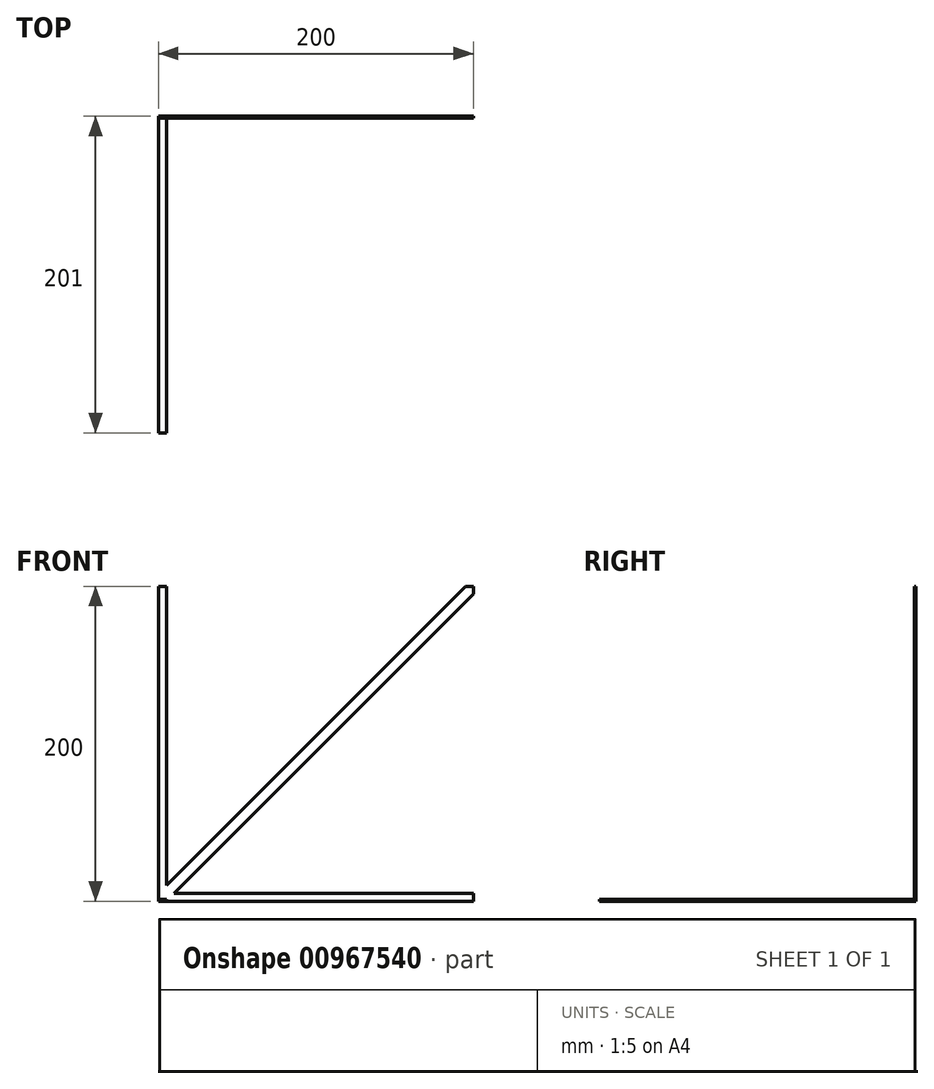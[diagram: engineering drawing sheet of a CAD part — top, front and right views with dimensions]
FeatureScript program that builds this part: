
annotation { "Feature Type Name" : "Feature", "Feature Type Description" : "" }
export const myFeature = defineFeature(function(context is Context, id is Id, definition is map)
    precondition{}
    {
        {
            var Q0;
            Q0=qCreatedBy(makeId("Front.planeOp"),FACE);
            var sketch = newSketch(context, id + "F0", { "sketchPlane" : qUnion([Q0])});
            skLineSegment(sketch, "E0.bottom", {"start": v(0, 0) * mm, "end": v(5, 0) * mm});
            skLineSegment(sketch, "E0.left", {"start": v(0, 0) * mm, "end": v(0, 5) * mm});
            skLineSegment(sketch, "E1", {"start": v(10, 5) * mm, "end": v(200, 195) * mm});
            skLineSegment(sketch, "E2", {"start": v(5, 10) * mm, "end": v(195, 200) * mm});
            skLineSegment(sketch, "E3", {"start": v(195, 200) * mm, "end": v(200, 200) * mm});
            skLineSegment(sketch, "E4", {"start": v(200, 200) * mm, "end": v(200, 195) * mm});
            skLineSegment(sketch, "E5", {"start": v(5, 0) * mm, "end": v(200, 0) * mm});
            skLineSegment(sketch, "E6", {"start": v(200, 0) * mm, "end": v(200, 5) * mm});
            skLineSegment(sketch, "E7", {"start": v(200, 5) * mm, "end": v(10, 5) * mm});
            skLineSegment(sketch, "E8", {"start": v(0, 5) * mm, "end": v(0, 200) * mm});
            skLineSegment(sketch, "E9", {"start": v(0, 200) * mm, "end": v(5, 200) * mm});
            skLineSegment(sketch, "E10", {"start": v(5, 200) * mm, "end": v(5, 10) * mm});
            skSolve(sketch);
        }
        {
            var Q0;
            Q0=makeQuery(id+"F0.imprint","IMPRINT",FACE,{"disambiguationData":[TD([[makeQuery(id+"F0.imprint","IMPRINT",EDGE,{"derivedFrom":sQuery(id+"F0.wireOp",EDGE,"E0.bottom")}),1.0]])]});
            extrude(context, id + "F1", {"entities" : qUnion([Q0]), "depth" : 1 * mm, "offsetDistance" : 25 * mm});
        }
        {
            var Q0;
            Q0=makeQuery(id+"F1.opExtrude","CAP_FACE",FACE,{"disambiguationData":[OSD([sQuery(id+"F0.wireOp",EDGE,"E0.bottom"),sQuery(id+"F0.wireOp",EDGE,"E0.left"),sQuery(id+"F0.wireOp",EDGE,"E1"),sQuery(id+"F0.wireOp",EDGE,"E2"),sQuery(id+"F0.wireOp",EDGE,"E3"),sQuery(id+"F0.wireOp",EDGE,"E4"),sQuery(id+"F0.wireOp",EDGE,"E5"),sQuery(id+"F0.wireOp",EDGE,"E6"),sQuery(id+"F0.wireOp",EDGE,"E7"),sQuery(id+"F0.wireOp",EDGE,"E8"),sQuery(id+"F0.wireOp",EDGE,"E9"),sQuery(id+"F0.wireOp",EDGE,"E10")])],"isStart":false});
            var sketch = newSketch(context, id + "F2", { "sketchPlane" : qUnion([Q0])});
            skLineSegment(sketch, "E11.bottom", {"start": v(0, 0) * mm, "end": v(5, 0) * mm});
            skLineSegment(sketch, "E11.top", {"start": v(0, 1) * mm, "end": v(5, 1) * mm});
            skLineSegment(sketch, "E11.left", {"start": v(0, 0) * mm, "end": v(0, 1) * mm});
            skLineSegment(sketch, "E11.right", {"start": v(5, 0) * mm, "end": v(5, 1) * mm});
            skSolve(sketch);
        }
        {
            var Q0;
            Q0=makeQuery(id+"F2.imprint","IMPRINT",FACE,{"disambiguationData":[TD([[makeQuery(id+"F2.imprint","IMPRINT",EDGE,{"derivedFrom":sQuery(id+"F2.wireOp",EDGE,"E11.bottom")}),1.0]])]});
            extrude(context, id + "F3", {"entities" : qUnion([Q0]), "operationType" : NewBodyOperationType.ADD, "depth" : 200 * mm, "offsetDistance" : 25 * mm});
        }
    });
